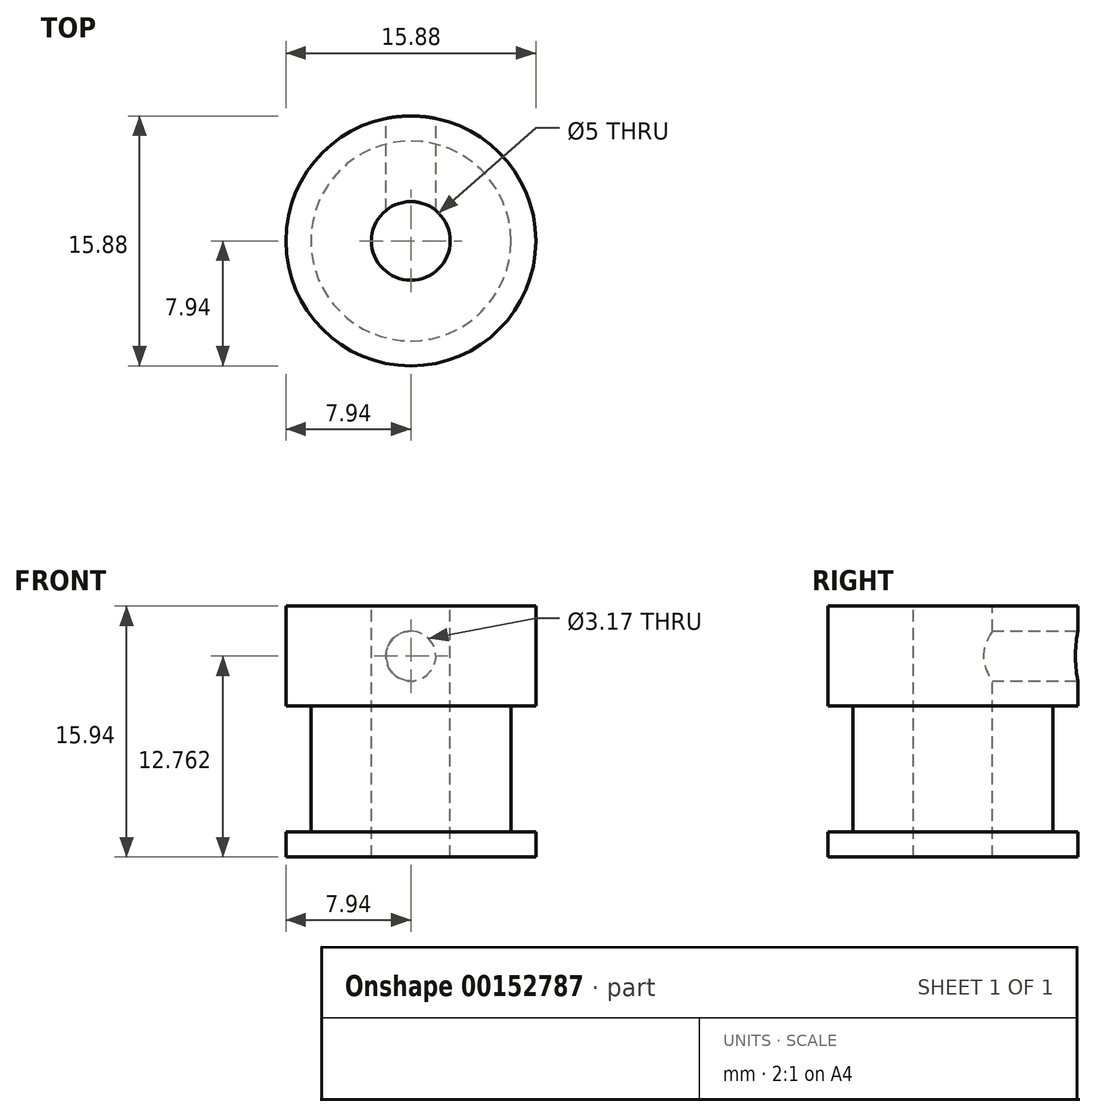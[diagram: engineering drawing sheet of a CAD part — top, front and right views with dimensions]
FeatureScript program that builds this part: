
annotation { "Feature Type Name" : "Feature", "Feature Type Description" : "" }
export const myFeature = defineFeature(function(context is Context, id is Id, definition is map)
    precondition{}
    {
        {
            var Q0;
            Q0=qCreatedBy(makeId("Top.planeOp"),FACE);
            var sketch = newSketch(context, id + "F0", { "sketchPlane" : qUnion([Q0])});
            skCircle(sketch, "E0", {"center": v(0, 0) * mm, "radius": 7.94 * mm});
            skSolve(sketch);
        }
        {
            var Q0;
            Q0=qSketchRegion(id+"F0",true);
            extrude(context, id + "F1", {"entities" : qUnion([Q0]), "depth" : 1.59 * mm});
        }
        {
            var Q0;
            Q0=makeQuery(id+"F1.opExtrude","CAP_FACE",FACE,{"disambiguationData":[OSD([sQuery(id+"F0.wireOp",EDGE,"E0")])],"isStart":false});
            var sketch = newSketch(context, id + "F2", { "sketchPlane" : qUnion([Q0])});
            skCircle(sketch, "E1", {"center": v(0, 0) * mm, "radius": 6.35 * mm});
            skSolve(sketch);
        }
        {
            var Q0;
            Q0=qSketchRegion(id+"F2",true);
            extrude(context, id + "F3", {"entities" : qUnion([Q0]), "operationType" : NewBodyOperationType.ADD, "depth" : 8 * mm});
        }
        {
            var Q0;
            Q0=makeQuery(id+"F3.opExtrude","CAP_FACE",FACE,{"disambiguationData":[OSD([sQuery(id+"F2.wireOp",EDGE,"E1")])],"isStart":false});
            var sketch = newSketch(context, id + "F4", { "sketchPlane" : qUnion([Q0])});
            skCircle(sketch, "E2", {"center": v(0, 0) * mm, "radius": 7.94 * mm, "construction": true});
            skLineSegment(sketch, "E3.bottom", {"start": v(7.94, -7.94) * mm, "end": v(-7.94, -7.94) * mm});
            skLineSegment(sketch, "E3.top", {"start": v(7.94, 7.94) * mm, "end": v(-7.94, 7.94) * mm});
            skLineSegment(sketch, "E3.left", {"start": v(7.94, -7.94) * mm, "end": v(7.94, 7.94) * mm});
            skLineSegment(sketch, "E3.right", {"start": v(-7.94, -7.94) * mm, "end": v(-7.94, 7.94) * mm});
            skSolve(sketch);
        }
        {
            var Q0;
            Q0=qSketchRegion(id+"F4",true);
            extrude(context, id + "F5", {"entities" : qUnion([Q0]), "operationType" : NewBodyOperationType.ADD, "depth" : 6.35 * mm});
        }
        {
            var Q0;
            Q0=makeQuery(id+"F5.opExtrude","CAP_FACE",FACE,{"disambiguationData":[OSD([sQuery(id+"F4.wireOp",EDGE,"E3.bottom"),sQuery(id+"F4.wireOp",EDGE,"E3.top"),sQuery(id+"F4.wireOp",EDGE,"E3.left"),sQuery(id+"F4.wireOp",EDGE,"E3.right")])],"isStart":false});
            var sketch = newSketch(context, id + "F6", { "sketchPlane" : qUnion([Q0])});
            skCircle(sketch, "E4", {"center": v(0, 0) * mm, "radius": 2.5 * mm});
            skSolve(sketch);
        }
        {
            var Q0;
            Q0=qSketchRegion(id+"F6",true);
            var Q1;
            Q1=makeQuery(id+"F1.opExtrude","CAP_FACE",FACE,{"disambiguationData":[OSD([sQuery(id+"F0.wireOp",EDGE,"E0")])],"isStart":true});
            extrude(context, id + "F7", {"entities" : qUnion([Q0]), "operationType" : NewBodyOperationType.REMOVE, "endBound" : BoundingType.UP_TO_SURFACE, "oppositeDirection" : true, "endBoundEntityFace" : qUnion([Q1]), "depth" : 25.4 * mm});
        }
        {
            var Q0;
            Q0=makeQuery(id+"F5.opExtrude","SWEPT_FACE",FACE,{"disambiguationData":[OSD([sQuery(id+"F4.wireOp",EDGE,"E3.top")])]});
            var sketch = newSketch(context, id + "F8", { "sketchPlane" : qUnion([Q0])});
            skLineSegment(sketch, "E5", {"start": v(0, 15.94) * mm, "end": v(0, 9.59) * mm, "construction": true});
            skCircle(sketch, "E6", {"center": v(0, 12.76) * mm, "radius": 1.59 * mm});
            skSolve(sketch);
        }
        {
            var Q0;
            Q0=qSketchRegion(id+"F8",true);
            var Q1;
            Q1=makeQuery(id+"F7.boolean.opBoolean","COPY",FACE,{"derivedFrom":makeQuery(id+"F7.opExtrude","SWEPT_FACE",FACE,{"disambiguationData":[OSD([sQuery(id+"F6.wireOp",EDGE,"E4")])]})});
            extrude(context, id + "F9", {"entities" : qUnion([Q0]), "operationType" : NewBodyOperationType.REMOVE, "endBound" : BoundingType.UP_TO_SURFACE, "oppositeDirection" : true, "endBoundEntityFace" : qUnion([Q1]), "depth" : 25.4 * mm});
        }
        {
            var Q0;
            Q0=makeQuery(id+"F5.opExtrude","SWEPT_EDGE",EDGE,{"disambiguationData":[OSD([sQuery(id+"F4.wireOp",EDGE,"E3.top"),sQuery(id+"F4.wireOp",EDGE,"E3.right")])]});
            var Q1;
            Q1=makeQuery(id+"F5.opExtrude","SWEPT_EDGE",EDGE,{"disambiguationData":[OSD([sQuery(id+"F4.wireOp",EDGE,"E3.bottom"),sQuery(id+"F4.wireOp",EDGE,"E3.right")])]});
            var Q2;
            Q2=makeQuery(id+"F5.opExtrude","SWEPT_EDGE",EDGE,{"disambiguationData":[OSD([sQuery(id+"F4.wireOp",EDGE,"E3.top"),sQuery(id+"F4.wireOp",EDGE,"E3.left")])]});
            var Q3;
            Q3=makeQuery(id+"F5.opExtrude","SWEPT_EDGE",EDGE,{"disambiguationData":[OSD([sQuery(id+"F4.wireOp",EDGE,"E3.bottom"),sQuery(id+"F4.wireOp",EDGE,"E3.left")])]});
            fillet(context, id + "F10", {"entities" : qUnion([Q0, Q1, Q2, Q3]), "radius" : 7.94 * mm, "tangentPropagation" : true, "allowEdgeOverflow" : false});
        }
    });
